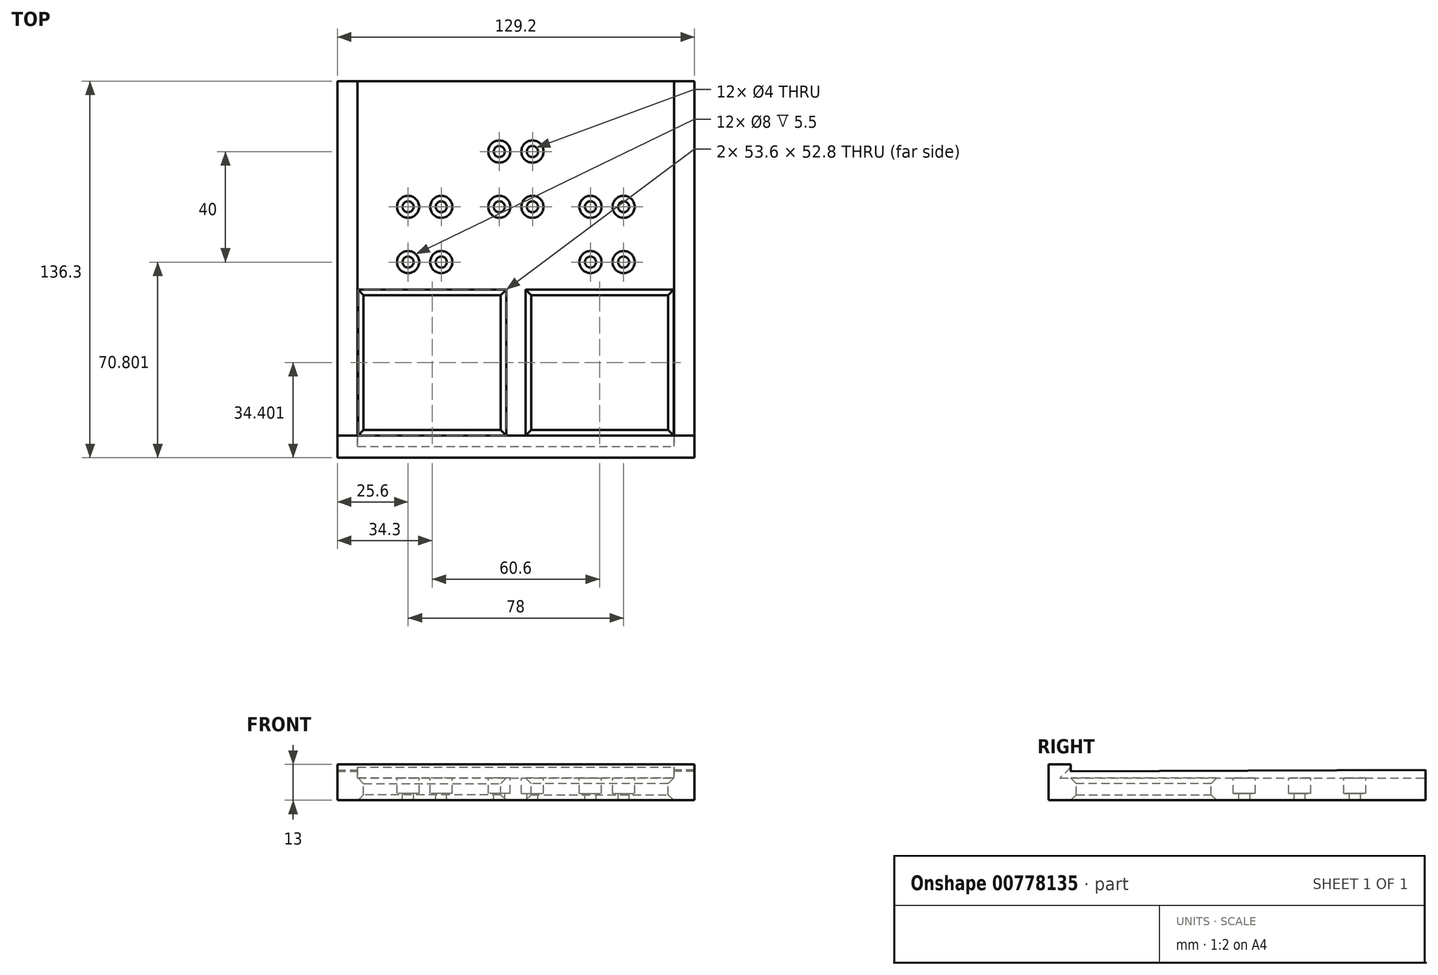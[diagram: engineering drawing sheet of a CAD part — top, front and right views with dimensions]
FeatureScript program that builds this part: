
annotation { "Feature Type Name" : "Feature", "Feature Type Description" : "" }
export const myFeature = defineFeature(function(context is Context, id is Id, definition is map)
    precondition{}
    {
        {
            var Q0;
            Q0=qCreatedBy(makeId("Top.planeOp"),FACE);
            var sketch = newSketch(context, id + "F0", { "sketchPlane" : qUnion([Q0])});
            skLineSegment(sketch, "E0", {"start": v(0, 83.15) * mm, "end": v(-64.6, 83.15) * mm});
            skLineSegment(sketch, "E1", {"start": v(-64.6, 83.15) * mm, "end": v(-64.6, -53.15) * mm});
            skLineSegment(sketch, "E2", {"start": v(-64.6, -53.15) * mm, "end": v(0, -53.15) * mm});
            skLineSegment(sketch, "E3", {"start": v(0, -53.15) * mm, "end": v(0, 83.15) * mm});
            skLineSegment(sketch, "E4", {"start": v(-64.6, -61.88) * mm, "end": v(-55.1, -61.88) * mm, "construction": true});
            skLineSegment(sketch, "E5", {"start": v(-73.9, -53.15) * mm, "end": v(-73.9, -43.15) * mm, "construction": true});
            skLineSegment(sketch, "E6", {"start": v(0, -59.13) * mm, "end": v(-5.5, -59.13) * mm, "construction": true});
            skLineSegment(sketch, "E7", {"start": v(-55.1, -43.15) * mm, "end": v(-5.5, -43.15) * mm});
            skLineSegment(sketch, "E8", {"start": v(-5.5, -43.15) * mm, "end": v(-5.5, 5.65) * mm});
            skLineSegment(sketch, "E9", {"start": v(-5.5, 5.65) * mm, "end": v(-55.1, 5.65) * mm});
            skLineSegment(sketch, "E10", {"start": v(-55.1, 5.65) * mm, "end": v(-55.1, -43.15) * mm});
            skLineSegment(sketch, "E11", {"start": v(9.34, -53.15) * mm, "end": v(9.34, 5.65) * mm, "construction": true});
            skSolve(sketch);
        }
        {
            var Q0;
            Q0 = qSketchRegion(id + "F0", true);
            extrude(context, id + "F1", {"entities" : qUnion([Q0]), "oppositeDirection" : true, "depth" : 13 * mm, "offsetDistance" : 25 * mm});
        }
        {
            var Q0;
            Q0=makeQuery(id+"F1.opExtrude","SWEPT_FACE",FACE,{"disambiguationData":[OSD([sQuery(id+"F0.wireOp",EDGE,"E3")])]});
            var sketch = newSketch(context, id + "F2", { "sketchPlane" : qUnion([Q0])});
            skLineSegment(sketch, "E12", {"start": v(-45.15, 0) * mm, "end": v(-45.15, -1) * mm});
            skLineSegment(sketch, "E13", {"start": v(-45.15, -1) * mm, "end": v(-49.15, -5) * mm});
            skLineSegment(sketch, "E14", {"start": v(-49.15, -5) * mm, "end": v(83.15, -5) * mm});
            skLineSegment(sketch, "E15", {"start": v(83.15, -5) * mm, "end": v(83.15, -13) * mm});
            skLineSegment(sketch, "E16", {"start": v(83.15, -13) * mm, "end": v(-53.15, -13) * mm});
            skLineSegment(sketch, "E17", {"start": v(-53.15, -13) * mm, "end": v(-53.15, 0) * mm});
            skLineSegment(sketch, "E18", {"start": v(-53.15, 0) * mm, "end": v(-45.15, 0) * mm});
            skLineSegment(sketch, "E19", {"start": v(-45.15, 0) * mm, "end": v(83.15, 0) * mm});
            skLineSegment(sketch, "E20", {"start": v(83.15, 0) * mm, "end": v(83.15, -5) * mm});
            skLineSegment(sketch, "E21", {"start": v(-58.94, -13) * mm, "end": v(-58.94, -5) * mm, "construction": true});
            skLineSegment(sketch, "E22", {"start": v(-58.94, -5) * mm, "end": v(-58.94, -1) * mm, "construction": true});
            skLineSegment(sketch, "E23", {"start": v(-58.94, -1) * mm, "end": v(-58.94, 0) * mm, "construction": true});
            skLineSegment(sketch, "E24", {"start": v(-53.15, 4.13) * mm, "end": v(-49.15, 4.13) * mm, "construction": true});
            skLineSegment(sketch, "E25", {"start": v(-49.15, 4.13) * mm, "end": v(-45.15, 4.13) * mm, "construction": true});
            skLineSegment(sketch, "E26", {"start": v(87.18, 0) * mm, "end": v(87.18, -2) * mm, "construction": true});
            skLineSegment(sketch, "E27", {"start": v(83.15, -2) * mm, "end": v(-45.15, -2.5) * mm});
            skPoint(sketch, "E27.endSnap0", {"position": v(83.15, -2.5) * mm});
            skLineSegment(sketch, "E28", {"start": v(-45.15, -2.5) * mm, "end": v(-45.15, -1) * mm});
            skSolve(sketch);
        }
        {
            var Q0;
            Q0=makeQuery(id+"F2.imprint","IMPRINT",FACE,{"disambiguationData":[TD([[makeQuery(id+"F2.imprint","IMPRINT",EDGE,{"derivedFrom":sQuery(id+"F2.wireOp",EDGE,"E13")}),1.0]])]});
            extrude(context, id + "F3", {"entities" : qUnion([Q0]), "operationType" : NewBodyOperationType.REMOVE, "oppositeDirection" : true, "depth" : 57.25 * mm, "offsetDistance" : 25 * mm});
        }
        {
            var Q0;
            Q0=makeQuery(id+"F2.imprint","IMPRINT",FACE,{"disambiguationData":[TD([[makeQuery(id+"F2.imprint","IMPRINT",EDGE,{"derivedFrom":sQuery(id+"F2.wireOp",EDGE,"E12")}),1.0]])]});
            extrude(context, id + "F4", {"entities" : qUnion([Q0]), "operationType" : NewBodyOperationType.REMOVE, "endBound" : BoundingType.UP_TO_NEXT, "oppositeDirection" : true, "depth" : 25 * mm, "offsetDistance" : 25 * mm});
        }
        {
            var Q0;
            Q0=makeQuery(id+"F3.boolean.opBoolean","COPY",EDGE,{"derivedFrom":makeQuery(id+"F3.opExtrude","CAP_EDGE",EDGE,{"disambiguationData":[OSD([sQuery(id+"F2.wireOp",EDGE,"E27")])],"isStart":false})});
            var Q1;
            Q1=makeQuery(id+"F3.boolean.opBoolean","INTERSECT",EDGE,{"derivedFrom":[makeQuery(id+"F1.opExtrude","SWEPT_FACE",FACE,{"disambiguationData":[OSD([sQuery(id+"F0.wireOp",EDGE,"E7")])]}),makeQuery(id+"F3.opExtrude","SWEPT_FACE",FACE,{"disambiguationData":[OSD([sQuery(id+"F2.wireOp",EDGE,"E14")])]})]});
            var Q2;
            Q2=makeQuery(id+"F3.boolean.opBoolean","INTERSECT",EDGE,{"derivedFrom":[makeQuery(id+"F1.opExtrude","SWEPT_FACE",FACE,{"disambiguationData":[OSD([sQuery(id+"F0.wireOp",EDGE,"E10")])]}),makeQuery(id+"F3.opExtrude","SWEPT_FACE",FACE,{"disambiguationData":[OSD([sQuery(id+"F2.wireOp",EDGE,"E14")])]})]});
            var Q3;
            Q3=makeQuery(id+"F3.boolean.opBoolean","INTERSECT",EDGE,{"derivedFrom":[makeQuery(id+"F1.opExtrude","SWEPT_FACE",FACE,{"disambiguationData":[OSD([sQuery(id+"F0.wireOp",EDGE,"E9")])]}),makeQuery(id+"F3.opExtrude","SWEPT_FACE",FACE,{"disambiguationData":[OSD([sQuery(id+"F2.wireOp",EDGE,"E14")])]})]});
            var Q4;
            Q4=makeQuery(id+"F3.boolean.opBoolean","INTERSECT",EDGE,{"derivedFrom":[makeQuery(id+"F1.opExtrude","SWEPT_FACE",FACE,{"disambiguationData":[OSD([sQuery(id+"F0.wireOp",EDGE,"E8")])]}),makeQuery(id+"F3.opExtrude","SWEPT_FACE",FACE,{"disambiguationData":[OSD([sQuery(id+"F2.wireOp",EDGE,"E14")])]})]});
            var Q5;
            Q5=makeQuery(id+"F1.opExtrude","CAP_EDGE",EDGE,{"disambiguationData":[OSD([sQuery(id+"F0.wireOp",EDGE,"E9")])],"isStart":false});
            var Q6;
            Q6=makeQuery(id+"F1.opExtrude","CAP_EDGE",EDGE,{"disambiguationData":[OSD([sQuery(id+"F0.wireOp",EDGE,"E10")])],"isStart":false});
            var Q7;
            Q7=makeQuery(id+"F1.opExtrude","CAP_EDGE",EDGE,{"disambiguationData":[OSD([sQuery(id+"F0.wireOp",EDGE,"E7")])],"isStart":false});
            var Q8;
            Q8=makeQuery(id+"F1.opExtrude","CAP_EDGE",EDGE,{"disambiguationData":[OSD([sQuery(id+"F0.wireOp",EDGE,"E8")])],"isStart":false});
            chamfer(context, id + "F5", {"entities" : qUnion([Q0, Q1, Q2, Q3, Q4, Q5, Q6, Q7, Q8]), "width" : 2 * mm, "tangentPropagation" : true});
        }
        {
            var Q0;
            Q0=makeQuery(id+"F3.boolean.opBoolean","COPY",FACE,{"derivedFrom":makeQuery(id+"F3.opExtrude","SWEPT_FACE",FACE,{"disambiguationData":[OSD([sQuery(id+"F2.wireOp",EDGE,"E14")])]})});
            var sketch = newSketch(context, id + "F6", { "sketchPlane" : qUnion([Q0])});
            skLineSegment(sketch, "E29.bottom", {"start": v(-27, 17.65) * mm, "end": v(-39, 17.65) * mm, "construction": true});
            skLineSegment(sketch, "E29.top", {"start": v(-27, 37.65) * mm, "end": v(-39, 37.65) * mm, "construction": true});
            skLineSegment(sketch, "E29.left", {"start": v(-27, 17.65) * mm, "end": v(-27, 37.65) * mm, "construction": true});
            skLineSegment(sketch, "E29.right", {"start": v(-39, 17.65) * mm, "end": v(-39, 37.65) * mm, "construction": true});
            skPoint(sketch, "E29.middle", {"position": v(-33, 27.65) * mm});
            skLineSegment(sketch, "E30", {"start": v(-27, 37.65) * mm, "end": v(0, 37.65) * mm, "construction": true});
            skLineSegment(sketch, "E31", {"start": v(-27, 37.65) * mm, "end": v(-27, 83.15) * mm, "construction": true});
            skLineSegment(sketch, "E32", {"start": v(-27, 17.65) * mm, "end": v(-6, 17.65) * mm, "construction": true});
            skLineSegment(sketch, "E33", {"start": v(-6, 37.65) * mm, "end": v(-6, 57.65) * mm, "construction": true});
            skCircle(sketch, "E34", {"center": v(-39, 37.65) * mm, "radius": 2 * mm});
            skCircle(sketch, "E35", {"center": v(-39, 37.65) * mm, "radius": 4 * mm});
            skCircle(sketch, "E36", {"center": v(-27, 37.65) * mm, "radius": 2 * mm});
            skCircle(sketch, "E37", {"center": v(-27, 37.65) * mm, "radius": 4 * mm});
            skCircle(sketch, "E38", {"center": v(-39, 17.65) * mm, "radius": 2 * mm});
            skCircle(sketch, "E39", {"center": v(-39, 17.65) * mm, "radius": 4 * mm});
            skCircle(sketch, "E40", {"center": v(-27, 17.65) * mm, "radius": 2 * mm});
            skCircle(sketch, "E41", {"center": v(-27, 17.65) * mm, "radius": 4 * mm});
            skCircle(sketch, "E42", {"center": v(-6, 57.65) * mm, "radius": 2 * mm});
            skCircle(sketch, "E43", {"center": v(-6, 57.65) * mm, "radius": 4 * mm});
            skCircle(sketch, "E44", {"center": v(-6, 37.65) * mm, "radius": 2 * mm});
            skCircle(sketch, "E45", {"center": v(-6, 37.65) * mm, "radius": 4 * mm});
            skSolve(sketch);
        }
        {
            var Q0;
            Q0=makeQuery(id+"F6.imprint","IMPRINT",FACE,{"disambiguationData":[TD([[makeQuery(id+"F6.imprint","IMPRINT",EDGE,{"derivedFrom":sQuery(id+"F6.wireOp",EDGE,"E42")}),1.0]])]});
            var Q1;
            Q1=makeQuery(id+"F6.imprint","IMPRINT",FACE,{"disambiguationData":[TD([[makeQuery(id+"F6.imprint","IMPRINT",EDGE,{"derivedFrom":sQuery(id+"F6.wireOp",EDGE,"E44")}),1.0]])]});
            var Q2;
            Q2=makeQuery(id+"F6.imprint","IMPRINT",FACE,{"disambiguationData":[TD([[makeQuery(id+"F6.imprint","IMPRINT",EDGE,{"derivedFrom":sQuery(id+"F6.wireOp",EDGE,"E36")}),1.0]])]});
            var Q3;
            Q3=makeQuery(id+"F6.imprint","IMPRINT",FACE,{"disambiguationData":[TD([[makeQuery(id+"F6.imprint","IMPRINT",EDGE,{"derivedFrom":sQuery(id+"F6.wireOp",EDGE,"E34")}),1.0]])]});
            var Q4;
            Q4=makeQuery(id+"F6.imprint","IMPRINT",FACE,{"disambiguationData":[TD([[makeQuery(id+"F6.imprint","IMPRINT",EDGE,{"derivedFrom":sQuery(id+"F6.wireOp",EDGE,"E38")}),1.0]])]});
            var Q5;
            Q5=makeQuery(id+"F6.imprint","IMPRINT",FACE,{"disambiguationData":[TD([[makeQuery(id+"F6.imprint","IMPRINT",EDGE,{"derivedFrom":sQuery(id+"F6.wireOp",EDGE,"E40")}),1.0]])]});
            extrude(context, id + "F7", {"entities" : qUnion([Q0, Q1, Q2, Q3, Q4, Q5]), "operationType" : NewBodyOperationType.REMOVE, "endBound" : BoundingType.UP_TO_NEXT, "oppositeDirection" : true, "depth" : 25 * mm, "offsetDistance" : 25 * mm});
        }
        {
            var Q0;
            Q0=makeQuery(id+"F6.imprint","IMPRINT",FACE,{"disambiguationData":[TD([[makeQuery(id+"F6.imprint","IMPRINT",EDGE,{"derivedFrom":sQuery(id+"F6.wireOp",EDGE,"E42")}),-1.0]])]});
            var Q1;
            Q1=makeQuery(id+"F6.imprint","IMPRINT",FACE,{"disambiguationData":[TD([[makeQuery(id+"F6.imprint","IMPRINT",EDGE,{"derivedFrom":sQuery(id+"F6.wireOp",EDGE,"E44")}),-1.0]])]});
            var Q2;
            Q2=makeQuery(id+"F6.imprint","IMPRINT",FACE,{"disambiguationData":[TD([[makeQuery(id+"F6.imprint","IMPRINT",EDGE,{"derivedFrom":sQuery(id+"F6.wireOp",EDGE,"E36")}),-1.0]])]});
            var Q3;
            Q3=makeQuery(id+"F6.imprint","IMPRINT",FACE,{"disambiguationData":[TD([[makeQuery(id+"F6.imprint","IMPRINT",EDGE,{"derivedFrom":sQuery(id+"F6.wireOp",EDGE,"E34")}),-1.0]])]});
            var Q4;
            Q4=makeQuery(id+"F6.imprint","IMPRINT",FACE,{"disambiguationData":[TD([[makeQuery(id+"F6.imprint","IMPRINT",EDGE,{"derivedFrom":sQuery(id+"F6.wireOp",EDGE,"E38")}),-1.0]])]});
            var Q5;
            Q5=makeQuery(id+"F6.imprint","IMPRINT",FACE,{"disambiguationData":[TD([[makeQuery(id+"F6.imprint","IMPRINT",EDGE,{"derivedFrom":sQuery(id+"F6.wireOp",EDGE,"E40")}),-1.0]])]});
            extrude(context, id + "F8", {"entities" : qUnion([Q0, Q1, Q2, Q3, Q4, Q5]), "operationType" : NewBodyOperationType.REMOVE, "oppositeDirection" : true, "depth" : 5.5 * mm, "offsetDistance" : 25 * mm});
        }
        {
            var Q0;
            Q0=makeQuery(id+"F1.opExtrude","SWEPT_BODY",BODY,{"disambiguationData":[OSD([sQuery(id+"F0.wireOp",EDGE,"E0"),sQuery(id+"F0.wireOp",EDGE,"E1"),sQuery(id+"F0.wireOp",EDGE,"E2"),sQuery(id+"F0.wireOp",EDGE,"E3")])]});
            var Q1;
            Q1=makeQuery(id+"F1.opExtrude","SWEPT_FACE",FACE,{"disambiguationData":[OSD([sQuery(id+"F0.wireOp",EDGE,"E3")])]});
            mirror(context, id + "F9", {"operationType" : NewBodyOperationType.ADD, "entities" : qUnion([Q0]), "mirrorPlane" : qUnion([Q1])});
        }
    });
